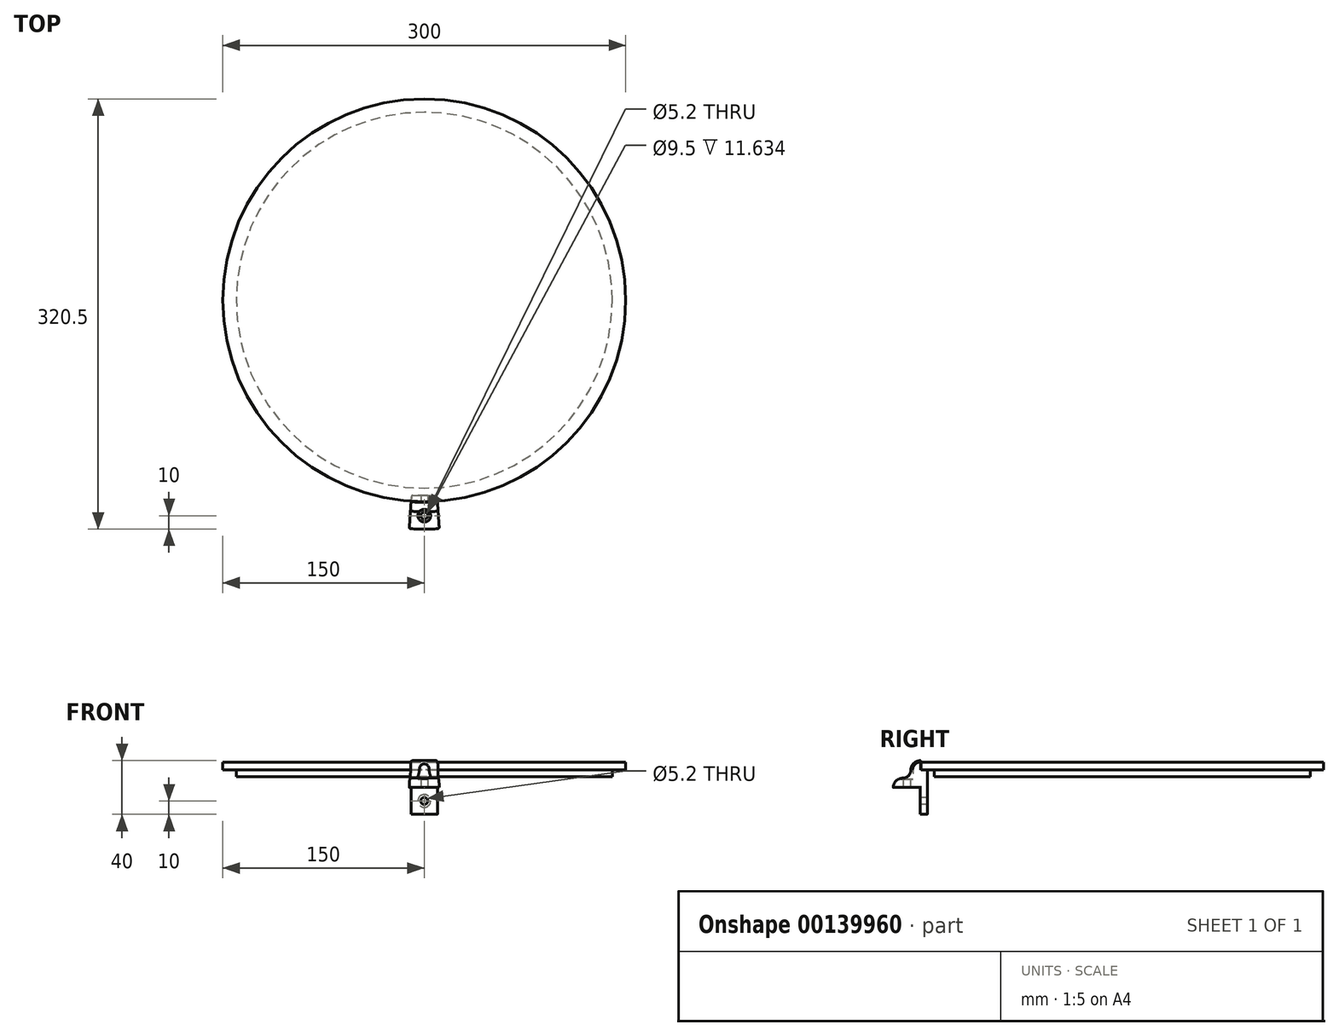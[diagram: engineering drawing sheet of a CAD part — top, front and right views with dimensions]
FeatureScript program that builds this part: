
annotation { "Feature Type Name" : "Feature", "Feature Type Description" : "" }
export const myFeature = defineFeature(function(context is Context, id is Id, definition is map)
    precondition{}
    {
        {
            var Q0;
            Q0=qCreatedBy(makeId("Top.planeOp"),FACE);
            var sketch = newSketch(context, id + "F0", { "sketchPlane" : qUnion([Q0])});
            skCircle(sketch, "E0", {"center": v(0, 0) * mm, "radius": 150 * mm});
            skCircle(sketch, "E1", {"center": v(0, 0) * mm, "radius": 140 * mm});
            skLineSegment(sketch, "E2", {"start": v(-260.67, -150.5) * mm, "end": v(0, 301) * mm, "construction": true});
            skLineSegment(sketch, "E3", {"start": v(0, 301) * mm, "end": v(260.67, -150.5) * mm, "construction": true});
            skLineSegment(sketch, "E4", {"start": v(260.67, -150.5) * mm, "end": v(-260.67, -150.5) * mm, "construction": true});
            skCircle(sketch, "E5", {"center": v(0, 0) * mm, "radius": 150.5 * mm, "construction": true});
            skPoint(sketch, "E6", {"position": v(-130.34, 75.25) * mm});
            skPoint(sketch, "E7", {"position": v(0, -150.5) * mm});
            skPoint(sketch, "E8", {"position": v(130.34, 75.25) * mm});
            skSolve(sketch);
        }
        {
            var Q0;
            Q0=makeQuery(id+"F0.imprint","IMPRINT",FACE,{"disambiguationData":[TD([[makeQuery(id+"F0.imprint","IMPRINT",EDGE,{"derivedFrom":sQuery(id+"F0.wireOp",EDGE,"E0")}),1.0]])]});
            var Q1;
            Q1=makeQuery(id+"F0.imprint","IMPRINT",FACE,{"disambiguationData":[TD([[makeQuery(id+"F0.imprint","IMPRINT",EDGE,{"derivedFrom":sQuery(id+"F0.wireOp",EDGE,"E1")}),1.0]])]});
            extrude(context, id + "F1", {"entities" : qUnion([Q0, Q1]), "depth" : 6 * mm, "offsetDistance" : 25 * mm});
        }
        {
            var Q0;
            Q0=makeQuery(id+"F0.imprint","IMPRINT",FACE,{"disambiguationData":[TD([[makeQuery(id+"F0.imprint","IMPRINT",EDGE,{"derivedFrom":sQuery(id+"F0.wireOp",EDGE,"E1")}),1.0]])]});
            extrude(context, id + "F2", {"entities" : qUnion([Q0]), "operationType" : NewBodyOperationType.ADD, "oppositeDirection" : true, "depth" : 5 * mm, "offsetDistance" : 25 * mm});
        }
        {
            var Q0;
            Q0=qCreatedBy(makeId("Right.planeOp"),FACE);
            var sketch = newSketch(context, id + "F3", { "sketchPlane" : qUnion([Q0])});
            skLineSegment(sketch, "E9", {"start": v(-150.5, 0) * mm, "end": v(-150.5, 7) * mm});
            skLineSegment(sketch, "E10", {"start": v(-170.5, -13) * mm, "end": v(-150.5, -13) * mm});
            skLineSegment(sketch, "E11", {"start": v(-150.5, -13) * mm, "end": v(-150.5, -33) * mm});
            skLineSegment(sketch, "E12", {"start": v(-145.5, -33) * mm, "end": v(-145.5, 0) * mm});
            skLineSegment(sketch, "E13", {"start": v(-145.5, 0) * mm, "end": v(-150.5, 0) * mm});
            skArc(sketch, "E14", {"start": v(-150.5, 7) * mm, "mid": v(-155.45, 4.95) * mm, "end": v(-157.5, 0) * mm});
            skArc(sketch, "E15", {"start": v(-163.5, -6) * mm, "mid": v(-168.45, -8.05) * mm, "end": v(-170.5, -13) * mm});
            skArc(sketch, "E16", {"start": v(-163.5, -6) * mm, "mid": v(-159.26, -4.24) * mm, "end": v(-157.5, 0) * mm});
            skLineSegment(sketch, "E17", {"start": v(-150.5, -33) * mm, "end": v(-170.5, -33) * mm});
            skLineSegment(sketch, "E18", {"start": v(-170.5, -33) * mm, "end": v(-170.5, -13) * mm});
            skLineSegment(sketch, "E19", {"start": v(-150.5, -33) * mm, "end": v(-145.5, -33) * mm});
            skSolve(sketch);
        }
        {
            var Q0;
            Q0=makeQuery(id+"F3.imprint","IMPRINT",FACE,{"disambiguationData":[TD([[makeQuery(id+"F3.imprint","IMPRINT",EDGE,{"derivedFrom":sQuery(id+"F3.wireOp",EDGE,"E9")}),1.0]])]});
            var Q1;
            Q1=makeQuery(id+"F3.imprint","IMPRINT",FACE,{"disambiguationData":[TD([[makeQuery(id+"F3.imprint","IMPRINT",EDGE,{"derivedFrom":sQuery(id+"F3.wireOp",EDGE,"E10")}),-1.0]])]});
            var Q2;
            Q2=sQuery(id+"F0.wireOp",EDGE,"E1");
            revolve(context, id + "F4", {"surfaceOperationType" : NewSurfaceOperationType.NEW, "entities" : qUnion([Q0, Q1]), "axis" : qUnion([Q2]), "revolveType" : RevolveType.SYMMETRIC, "angle" : 7.5 * degree});
        }
        {
            var Q0;
            Q0=makeQuery(id+"F3.imprint","IMPRINT",FACE,{"disambiguationData":[TD([[makeQuery(id+"F3.imprint","IMPRINT",EDGE,{"derivedFrom":sQuery(id+"F3.wireOp",EDGE,"E10")}),-1.0]])]});
            extrude(context, id + "F5", {"entities" : qUnion([Q0]), "operationType" : NewBodyOperationType.REMOVE, "oppositeDirection" : true, "depth" : 25 * mm, "offsetDistance" : 25 * mm, "symmetric" : true});
        }
        {
            var Q0;
            Q0=makeQuery(id+"F5.boolean.opBoolean","COPY",FACE,{"derivedFrom":makeQuery(id+"F5.opExtrude","SWEPT_FACE",FACE,{"disambiguationData":[OSD([sQuery(id+"F3.wireOp",EDGE,"E11")])]})});
            var sketch = newSketch(context, id + "F6", { "sketchPlane" : qUnion([Q0])});
            skCircle(sketch, "E20", {"center": v(0, -23) * mm, "radius": 2.6 * mm});
            skCircle(sketch, "E21", {"center": v(0, -23) * mm, "radius": 4.75 * mm});
            skSolve(sketch);
        }
        {
            var Q0;
            Q0=makeQuery(id+"F5.boolean.opBoolean","COPY",FACE,{"derivedFrom":makeQuery(id+"F5.opExtrude","SWEPT_FACE",FACE,{"disambiguationData":[OSD([sQuery(id+"F3.wireOp",EDGE,"E10")])]})});
            var sketch = newSketch(context, id + "F7", { "sketchPlane" : qUnion([Q0])});
            skCircle(sketch, "E22", {"center": v(0, 160.5) * mm, "radius": 2.6 * mm});
            skCircle(sketch, "E23", {"center": v(0, 160.5) * mm, "radius": 4.75 * mm});
            skSolve(sketch);
        }
        {
            var Q0;
            Q0=makeQuery(id+"F6.imprint","IMPRINT",FACE,{"disambiguationData":[TD([[makeQuery(id+"F6.imprint","IMPRINT",EDGE,{"derivedFrom":sQuery(id+"F6.wireOp",EDGE,"E20")}),1.0]])]});
            var Q1;
            Q1=sQuery(id+"F6.wireOp",EDGE,"E20");
            var Q2;
            Q2=sQuery(id+"F7.wireOp",EDGE,"E22");
            extrude(context, id + "F8", {"entities" : qUnion([Q0]), "operationType" : NewBodyOperationType.REMOVE, "surfaceEntities" : qUnion([Q1, Q2]), "oppositeDirection" : true, "depth" : 25 * mm, "offsetDistance" : 25 * mm});
        }
        {
            var Q0;
            Q0=makeQuery(id+"F7.imprint","IMPRINT",FACE,{"disambiguationData":[TD([[makeQuery(id+"F7.imprint","IMPRINT",EDGE,{"derivedFrom":sQuery(id+"F7.wireOp",EDGE,"E22")}),1.0]])]});
            var Q1;
            Q1=sQuery(id+"F7.wireOp",EDGE,"E22");
            extrude(context, id + "F9", {"entities" : qUnion([Q0]), "operationType" : NewBodyOperationType.REMOVE, "surfaceEntities" : qUnion([Q1]), "oppositeDirection" : true, "depth" : 25 * mm, "offsetDistance" : 25 * mm});
        }
        {
            var Q0;
            Q0=makeQuery(id+"F7.imprint","IMPRINT",FACE,{"disambiguationData":[TD([[makeQuery(id+"F7.imprint","IMPRINT",EDGE,{"derivedFrom":sQuery(id+"F7.wireOp",EDGE,"E22")}),-1.0]])]});
            var Q1;
            Q1=sQuery(id+"F7.wireOp",EDGE,"E23");
            extrude(context, id + "F10", {"entities" : qUnion([Q0]), "operationType" : NewBodyOperationType.REMOVE, "surfaceEntities" : qUnion([Q1]), "oppositeDirection" : true, "depth" : 25 * mm, "offsetDistance" : 25 * mm, "hasSecondDirection" : true, "secondDirectionOppositeDirection" : true, "secondDirectionDepth" : 6 * mm});
        }
        {
            var Q0;
            Q0=makeQuery(id+"F6.imprint","IMPRINT",FACE,{"disambiguationData":[TD([[makeQuery(id+"F6.imprint","IMPRINT",EDGE,{"derivedFrom":sQuery(id+"F6.wireOp",EDGE,"E20")}),-1.0]])]});
            extrude(context, id + "F11", {"entities" : qUnion([Q0]), "operationType" : NewBodyOperationType.REMOVE, "oppositeDirection" : true, "depth" : 25 * mm, "offsetDistance" : 25 * mm, "hasSecondDirection" : true, "secondDirectionOppositeDirection" : true, "secondDirectionDepth" : 5 * mm});
        }
        {
            var Q0;
            Q0=makeQuery(id+"F4.opRevolve","CAP_EDGE",EDGE,{"disambiguationData":[OSD([sQuery(id+"F3.wireOp",EDGE,"E12")])],"isStart":true});
            var Q1;
            Q1=makeQuery(id+"F4.opRevolve","CAP_EDGE",EDGE,{"disambiguationData":[OSD([sQuery(id+"F3.wireOp",EDGE,"E12")])],"isStart":false});
            var Q2;
            Q2=makeQuery(id+"F5.boolean.opBoolean","INTERSECT",EDGE,{"derivedFrom":[makeQuery(id+"F4.opRevolve","CAP_FACE",FACE,{"disambiguationData":[OSD([sQuery(id+"F3.wireOp",EDGE,"E9"),sQuery(id+"F3.wireOp",EDGE,"E12"),sQuery(id+"F3.wireOp",EDGE,"E13"),sQuery(id+"F3.wireOp",EDGE,"E14"),sQuery(id+"F3.wireOp",EDGE,"E15"),sQuery(id+"F3.wireOp",EDGE,"E16"),sQuery(id+"F3.wireOp",EDGE,"E17"),sQuery(id+"F3.wireOp",EDGE,"E18"),sQuery(id+"F3.wireOp",EDGE,"E19")])],"isStart":false}),makeQuery(id+"F5.opExtrude","SWEPT_FACE",FACE,{"disambiguationData":[OSD([sQuery(id+"F3.wireOp",EDGE,"E11")])]})]});
            var Q3;
            Q3=makeQuery(id+"F5.boolean.opBoolean","INTERSECT",EDGE,{"derivedFrom":[makeQuery(id+"F4.opRevolve","CAP_FACE",FACE,{"disambiguationData":[OSD([sQuery(id+"F3.wireOp",EDGE,"E9"),sQuery(id+"F3.wireOp",EDGE,"E12"),sQuery(id+"F3.wireOp",EDGE,"E13"),sQuery(id+"F3.wireOp",EDGE,"E14"),sQuery(id+"F3.wireOp",EDGE,"E15"),sQuery(id+"F3.wireOp",EDGE,"E16"),sQuery(id+"F3.wireOp",EDGE,"E17"),sQuery(id+"F3.wireOp",EDGE,"E18"),sQuery(id+"F3.wireOp",EDGE,"E19")])],"isStart":true}),makeQuery(id+"F5.opExtrude","SWEPT_FACE",FACE,{"disambiguationData":[OSD([sQuery(id+"F3.wireOp",EDGE,"E11")])]})]});
            var Q4;
            Q4=makeQuery(id+"F4.opRevolve","CAP_EDGE",EDGE,{"disambiguationData":[OSD([sQuery(id+"F3.wireOp",EDGE,"E15")])],"isStart":true});
            var Q5;
            Q5=makeQuery(id+"F4.opRevolve","CAP_EDGE",EDGE,{"disambiguationData":[OSD([sQuery(id+"F3.wireOp",EDGE,"E15")])],"isStart":false});
            fillet(context, id + "F12", {"entities" : qUnion([Q0, Q1, Q2, Q3, Q4, Q5]), "tangentPropagation" : true, "radius" : 1 * mm, "defaultsChanged" : false, "vertexSettings" : [], "allowEdgeOverflow" : false});
        }
    });
